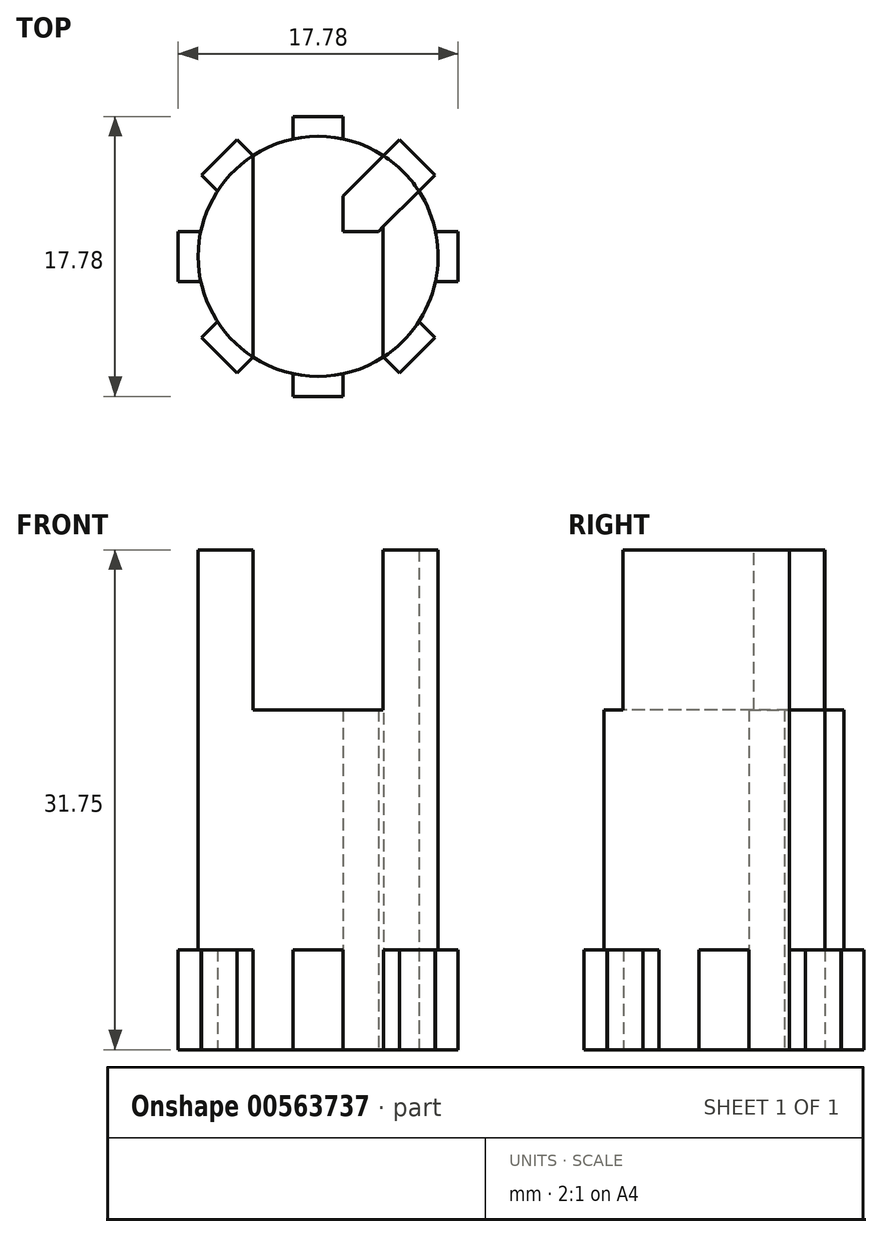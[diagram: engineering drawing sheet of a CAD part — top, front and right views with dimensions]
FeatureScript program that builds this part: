
annotation { "Feature Type Name" : "Feature", "Feature Type Description" : "" }
export const myFeature = defineFeature(function(context is Context, id is Id, definition is map)
    precondition{}
    {
        {
            var Q0;
            Q0=qCreatedBy(makeId("Top.planeOp"),FACE);
            var sketch = newSketch(context, id + "F0", { "sketchPlane" : qUnion([Q0])});
            skCircle(sketch, "E0", {"center": v(0, 0) * mm, "radius": 7.62 * mm});
            skLineSegment(sketch, "E1.bottom", {"start": v(8.9, 1.59) * mm, "end": v(-8.9, 1.59) * mm});
            skLineSegment(sketch, "E1.top", {"start": v(8.89, -1.59) * mm, "end": v(-8.89, -1.59) * mm});
            skLineSegment(sketch, "E1.left", {"start": v(8.9, 1.59) * mm, "end": v(8.9, -1.59) * mm});
            skLineSegment(sketch, "E1.right", {"start": v(-8.89, 1.59) * mm, "end": v(-8.89, -1.59) * mm});
            skLineSegment(sketch, "E2.1.0", {"start": v(7.4, -5.16) * mm, "end": v(5.16, -7.4) * mm});
            skLineSegment(sketch, "E2.1.1", {"start": v(-5.16, 7.4) * mm, "end": v(-7.4, 5.16) * mm});
            skLineSegment(sketch, "E2.1.2", {"start": v(7.4, -5.16) * mm, "end": v(-5.16, 7.4) * mm});
            skLineSegment(sketch, "E2.1.4", {"start": v(5.16, -7.4) * mm, "end": v(-7.4, 5.16) * mm});
            skLineSegment(sketch, "E2.2.0", {"start": v(1.59, -8.9) * mm, "end": v(-1.59, -8.89) * mm});
            skLineSegment(sketch, "E2.2.1", {"start": v(1.59, 8.89) * mm, "end": v(-1.59, 8.9) * mm});
            skLineSegment(sketch, "E2.2.2", {"start": v(1.59, -8.9) * mm, "end": v(1.59, 8.89) * mm});
            skLineSegment(sketch, "E2.2.4", {"start": v(-1.59, -8.89) * mm, "end": v(-1.59, 8.9) * mm});
            skLineSegment(sketch, "E2.3.0", {"start": v(-5.16, -7.4) * mm, "end": v(-7.4, -5.16) * mm});
            skLineSegment(sketch, "E2.3.1", {"start": v(7.4, 5.16) * mm, "end": v(5.16, 7.4) * mm});
            skLineSegment(sketch, "E2.3.2", {"start": v(-5.16, -7.4) * mm, "end": v(7.4, 5.16) * mm});
            skLineSegment(sketch, "E2.3.4", {"start": v(-7.4, -5.16) * mm, "end": v(5.16, 7.4) * mm});
            skLineSegment(sketch, "E2.anchor1", {"start": v(0, 0) * mm, "end": v(-8.9, -1.59) * mm, "construction": true});
            skLineSegment(sketch, "E2.anchor2", {"start": v(0, 0) * mm, "end": v(5.16, 7.4) * mm, "construction": true});
            skSolve(sketch);
        }
        {
            var Q0;
            Q0=makeQuery(id+"F0.imprint","IMPRINT",FACE,{"disambiguationData":[TD([[makeQuery(id+"F0.imprint","IMPRINT",EDGE,{"derivedFrom":sQuery(id+"F0.wireOp",EDGE,"E0")}),1.0]])]});
            var Q1;
            {var subQ0=sQuery(id+"F0.wireOp",EDGE,"E1.bottom");var subQ1=sQuery(id+"F0.wireOp",EDGE,"E0");var subQ2=makeQuery(id+"F0.imprint","INTERSECT",VERTEX,{"disambiguationData":[OD(0.0)],"derivedFrom":[subQ1,subQ0]});Q1=makeQuery(id+"F0.imprint","IMPRINT",FACE,{"disambiguationData":[TD([[makeQuery(id+"F0.imprint","IMPRINT",EDGE,{"disambiguationData":[TD([[subQ2,1.0]])],"derivedFrom":subQ1}),1.0]])]});}
            var Q2;
            {var subQ0=sQuery(id+"F0.wireOp",EDGE,"E1.top");var subQ1=sQuery(id+"F0.wireOp",EDGE,"E0");var subQ2=makeQuery(id+"F0.imprint","INTERSECT",VERTEX,{"disambiguationData":[OD(0.0)],"derivedFrom":[subQ1,subQ0]});Q2=makeQuery(id+"F0.imprint","IMPRINT",FACE,{"disambiguationData":[TD([[makeQuery(id+"F0.imprint","IMPRINT",EDGE,{"disambiguationData":[TD([[subQ2,-1.0]])],"derivedFrom":subQ1}),1.0]])]});}
            var Q3;
            {var subQ1=sQuery(id+"F0.wireOp",EDGE,"E0");var subQ7=sQuery(id+"F0.wireOp",EDGE,"E2.1.4");var subQ9=makeQuery(id+"F0.imprint","INTERSECT",VERTEX,{"disambiguationData":[OD(1.0)],"derivedFrom":[subQ1,subQ7]});Q3=makeQuery(id+"F0.imprint","IMPRINT",FACE,{"disambiguationData":[TD([[makeQuery(id+"F0.imprint","IMPRINT",EDGE,{"disambiguationData":[TD([[subQ9,-1.0]])],"derivedFrom":subQ1}),1.0]])]});}
            var Q4;
            {var subQ0=sQuery(id+"F0.wireOp",EDGE,"E2.2.4");var subQ1=sQuery(id+"F0.wireOp",EDGE,"E0");var subQ2=makeQuery(id+"F0.imprint","INTERSECT",VERTEX,{"disambiguationData":[OD(1.0)],"derivedFrom":[subQ1,subQ0]});Q4=makeQuery(id+"F0.imprint","IMPRINT",FACE,{"disambiguationData":[TD([[makeQuery(id+"F0.imprint","IMPRINT",EDGE,{"disambiguationData":[TD([[subQ2,-1.0]])],"derivedFrom":subQ1}),1.0]])]});}
            var Q5;
            {var subQ3=sQuery(id+"F0.wireOp",EDGE,"E2.3.4");var subQ5=sQuery(id+"F0.wireOp",EDGE,"E0");var subQ6=makeQuery(id+"F0.imprint","INTERSECT",VERTEX,{"disambiguationData":[OD(1.0)],"derivedFrom":[subQ5,subQ3]});Q5=makeQuery(id+"F0.imprint","IMPRINT",FACE,{"disambiguationData":[TD([[makeQuery(id+"F0.imprint","IMPRINT",EDGE,{"disambiguationData":[TD([[subQ6,-1.0]])],"derivedFrom":subQ5}),1.0]])]});}
            var Q6;
            {var subQ1=sQuery(id+"F0.wireOp",EDGE,"E1.bottom");var subQ5=sQuery(id+"F0.wireOp",EDGE,"E0");var subQ6=makeQuery(id+"F0.imprint","INTERSECT",VERTEX,{"disambiguationData":[OD(1.0)],"derivedFrom":[subQ5,subQ1]});Q6=makeQuery(id+"F0.imprint","IMPRINT",FACE,{"disambiguationData":[TD([[makeQuery(id+"F0.imprint","IMPRINT",EDGE,{"disambiguationData":[TD([[subQ6,-1.0]])],"derivedFrom":subQ5}),1.0]])]});}
            var Q7;
            {var subQ1=sQuery(id+"F0.wireOp",EDGE,"E0");var subQ7=sQuery(id+"F0.wireOp",EDGE,"E2.1.2");var subQ8=makeQuery(id+"F0.imprint","INTERSECT",VERTEX,{"disambiguationData":[OD(0.0)],"derivedFrom":[subQ1,subQ7]});Q7=makeQuery(id+"F0.imprint","IMPRINT",FACE,{"disambiguationData":[TD([[makeQuery(id+"F0.imprint","IMPRINT",EDGE,{"disambiguationData":[TD([[subQ8,-1.0]])],"derivedFrom":subQ1}),1.0]])]});}
            var Q8;
            {var subQ0=sQuery(id+"F0.wireOp",EDGE,"E2.2.2");var subQ1=sQuery(id+"F0.wireOp",EDGE,"E0");var subQ2=makeQuery(id+"F0.imprint","INTERSECT",VERTEX,{"disambiguationData":[OD(0.0)],"derivedFrom":[subQ1,subQ0]});Q8=makeQuery(id+"F0.imprint","IMPRINT",FACE,{"disambiguationData":[TD([[makeQuery(id+"F0.imprint","IMPRINT",EDGE,{"disambiguationData":[TD([[subQ2,-1.0]])],"derivedFrom":subQ1}),1.0]])]});}
            var Q9;
            {var subQ0=sQuery(id+"F0.wireOp",EDGE,"E2.3.2");var subQ1=sQuery(id+"F0.wireOp",EDGE,"E0");var subQ2=makeQuery(id+"F0.imprint","INTERSECT",VERTEX,{"disambiguationData":[OD(0.0)],"derivedFrom":[subQ1,subQ0]});Q9=makeQuery(id+"F0.imprint","IMPRINT",FACE,{"disambiguationData":[TD([[makeQuery(id+"F0.imprint","IMPRINT",EDGE,{"disambiguationData":[TD([[subQ2,-1.0]])],"derivedFrom":subQ1}),1.0]])]});}
            var Q10;
            {var subQ0=sQuery(id+"F0.wireOp",EDGE,"E2.2.2");var subQ1=sQuery(id+"F0.wireOp",EDGE,"E1.top");var subQ2=makeQuery(id+"F0.imprint","INTERSECT",VERTEX,{"derivedFrom":[subQ1,subQ0]});Q10=makeQuery(id+"F0.imprint","IMPRINT",FACE,{"disambiguationData":[TD([[makeQuery(id+"F0.imprint","IMPRINT",EDGE,{"disambiguationData":[TD([[subQ2,-1.0]])],"derivedFrom":subQ1}),1.0]])]});}
            var Q11;
            {var subQ0=sQuery(id+"F0.wireOp",EDGE,"E2.1.2");var subQ1=sQuery(id+"F0.wireOp",EDGE,"E1.top");var subQ2=makeQuery(id+"F0.imprint","INTERSECT",VERTEX,{"derivedFrom":[subQ1,subQ0]});Q11=makeQuery(id+"F0.imprint","IMPRINT",FACE,{"disambiguationData":[TD([[makeQuery(id+"F0.imprint","IMPRINT",EDGE,{"disambiguationData":[TD([[subQ2,-1.0]])],"derivedFrom":subQ1}),-1.0]])]});}
            var Q12;
            {var subQ0=sQuery(id+"F0.wireOp",EDGE,"E2.3.2");var subQ1=sQuery(id+"F0.wireOp",EDGE,"E1.bottom");var subQ2=makeQuery(id+"F0.imprint","INTERSECT",VERTEX,{"derivedFrom":[subQ1,subQ0]});Q12=makeQuery(id+"F0.imprint","IMPRINT",FACE,{"disambiguationData":[TD([[makeQuery(id+"F0.imprint","IMPRINT",EDGE,{"disambiguationData":[TD([[subQ2,-1.0]])],"derivedFrom":subQ1}),1.0]])]});}
            var Q13;
            {var subQ0=sQuery(id+"F0.wireOp",EDGE,"E2.2.2");var subQ1=sQuery(id+"F0.wireOp",EDGE,"E1.bottom");var subQ2=makeQuery(id+"F0.imprint","INTERSECT",VERTEX,{"derivedFrom":[subQ1,subQ0]});Q13=makeQuery(id+"F0.imprint","IMPRINT",FACE,{"disambiguationData":[TD([[makeQuery(id+"F0.imprint","IMPRINT",EDGE,{"disambiguationData":[TD([[subQ2,-1.0]])],"derivedFrom":subQ1}),-1.0]])]});}
            var Q14;
            {var subQ0=sQuery(id+"F0.wireOp",EDGE,"E2.2.4");var subQ1=sQuery(id+"F0.wireOp",EDGE,"E1.bottom");var subQ2=makeQuery(id+"F0.imprint","INTERSECT",VERTEX,{"derivedFrom":[subQ1,subQ0]});Q14=makeQuery(id+"F0.imprint","IMPRINT",FACE,{"disambiguationData":[TD([[makeQuery(id+"F0.imprint","IMPRINT",EDGE,{"disambiguationData":[TD([[subQ2,-1.0]])],"derivedFrom":subQ1}),1.0]])]});}
            var Q15;
            {var subQ0=sQuery(id+"F0.wireOp",EDGE,"E2.2.4");var subQ1=sQuery(id+"F0.wireOp",EDGE,"E1.top");var subQ2=makeQuery(id+"F0.imprint","INTERSECT",VERTEX,{"derivedFrom":[subQ1,subQ0]});Q15=makeQuery(id+"F0.imprint","IMPRINT",FACE,{"disambiguationData":[TD([[makeQuery(id+"F0.imprint","IMPRINT",EDGE,{"disambiguationData":[TD([[subQ2,-1.0]])],"derivedFrom":subQ1}),-1.0]])]});}
            var Q16;
            {var subQ0=sQuery(id+"F0.wireOp",EDGE,"E2.1.4");var subQ1=sQuery(id+"F0.wireOp",EDGE,"E1.top");var subQ2=makeQuery(id+"F0.imprint","INTERSECT",VERTEX,{"derivedFrom":[subQ1,subQ0]});Q16=makeQuery(id+"F0.imprint","IMPRINT",FACE,{"disambiguationData":[TD([[makeQuery(id+"F0.imprint","IMPRINT",EDGE,{"disambiguationData":[TD([[subQ2,-1.0]])],"derivedFrom":subQ1}),1.0]])]});}
            var Q17;
            {var subQ0=sQuery(id+"F0.wireOp",EDGE,"E2.1.4");var subQ1=sQuery(id+"F0.wireOp",EDGE,"E1.top");var subQ2=makeQuery(id+"F0.imprint","INTERSECT",VERTEX,{"derivedFrom":[subQ1,subQ0]});Q17=makeQuery(id+"F0.imprint","IMPRINT",FACE,{"disambiguationData":[TD([[makeQuery(id+"F0.imprint","IMPRINT",EDGE,{"disambiguationData":[TD([[subQ2,-1.0]])],"derivedFrom":subQ1}),-1.0]])]});}
            var Q18;
            {var subQ8=sQuery(id+"F0.wireOp",EDGE,"E2.1.2");var subQ11=sQuery(id+"F0.wireOp",EDGE,"E1.bottom");var subQ12=makeQuery(id+"F0.imprint","INTERSECT",VERTEX,{"derivedFrom":[subQ11,subQ8]});Q18=makeQuery(id+"F0.imprint","IMPRINT",FACE,{"disambiguationData":[TD([[makeQuery(id+"F0.imprint","IMPRINT",EDGE,{"disambiguationData":[TD([[subQ12,-1.0]])],"derivedFrom":subQ11}),1.0]])]});}
            var Q19;
            {var subQ0=sQuery(id+"F0.wireOp",EDGE,"E2.2.2");var subQ1=sQuery(id+"F0.wireOp",EDGE,"E1.top");var subQ2=makeQuery(id+"F0.imprint","INTERSECT",VERTEX,{"derivedFrom":[subQ1,subQ0]});Q19=makeQuery(id+"F0.imprint","IMPRINT",FACE,{"disambiguationData":[TD([[makeQuery(id+"F0.imprint","IMPRINT",EDGE,{"disambiguationData":[TD([[subQ2,-1.0]])],"derivedFrom":subQ1}),-1.0]])]});}
            var Q20;
            {var subQ0=sQuery(id+"F0.wireOp",EDGE,"E2.3.2");var subQ1=sQuery(id+"F0.wireOp",EDGE,"E2.1.2");var subQ2=makeQuery(id+"F0.imprint","INTERSECT",VERTEX,{"derivedFrom":[subQ1,subQ0]});Q20=makeQuery(id+"F0.imprint","IMPRINT",FACE,{"disambiguationData":[TD([[makeQuery(id+"F0.imprint","IMPRINT",EDGE,{"disambiguationData":[TD([[subQ2,-1.0]])],"derivedFrom":subQ1}),1.0]])]});}
            var Q21;
            {var subQ0=sQuery(id+"F0.wireOp",EDGE,"E2.2.2");var subQ1=sQuery(id+"F0.wireOp",EDGE,"E1.bottom");var subQ2=makeQuery(id+"F0.imprint","INTERSECT",VERTEX,{"derivedFrom":[subQ1,subQ0]});Q21=makeQuery(id+"F0.imprint","IMPRINT",FACE,{"disambiguationData":[TD([[makeQuery(id+"F0.imprint","IMPRINT",EDGE,{"disambiguationData":[TD([[subQ2,-1.0]])],"derivedFrom":subQ1}),1.0]])]});}
            var Q22;
            {var subQ0=sQuery(id+"F0.wireOp",EDGE,"E2.3.4");var subQ1=sQuery(id+"F0.wireOp",EDGE,"E1.bottom");var subQ2=makeQuery(id+"F0.imprint","INTERSECT",VERTEX,{"derivedFrom":[subQ1,subQ0]});Q22=makeQuery(id+"F0.imprint","IMPRINT",FACE,{"disambiguationData":[TD([[makeQuery(id+"F0.imprint","IMPRINT",EDGE,{"disambiguationData":[TD([[subQ2,-1.0]])],"derivedFrom":subQ1}),-1.0]])]});}
            var Q23;
            {var subQ0=sQuery(id+"F0.wireOp",EDGE,"E2.3.4");var subQ1=sQuery(id+"F0.wireOp",EDGE,"E1.bottom");var subQ2=makeQuery(id+"F0.imprint","INTERSECT",VERTEX,{"derivedFrom":[subQ1,subQ0]});Q23=makeQuery(id+"F0.imprint","IMPRINT",FACE,{"disambiguationData":[TD([[makeQuery(id+"F0.imprint","IMPRINT",EDGE,{"disambiguationData":[TD([[subQ2,-1.0]])],"derivedFrom":subQ1}),1.0]])]});}
            var Q24;
            {var subQ0=sQuery(id+"F0.wireOp",EDGE,"E2.1.2");var subQ1=sQuery(id+"F0.wireOp",EDGE,"E1.bottom");var subQ2=makeQuery(id+"F0.imprint","INTERSECT",VERTEX,{"derivedFrom":[subQ1,subQ0]});Q24=makeQuery(id+"F0.imprint","IMPRINT",FACE,{"disambiguationData":[TD([[makeQuery(id+"F0.imprint","IMPRINT",EDGE,{"disambiguationData":[TD([[subQ2,-1.0]])],"derivedFrom":subQ1}),-1.0]])]});}
            var Q25;
            {var subQ0=sQuery(id+"F0.wireOp",EDGE,"E2.2.4");var subQ1=sQuery(id+"F0.wireOp",EDGE,"E2.1.4");var subQ2=makeQuery(id+"F0.imprint","INTERSECT",VERTEX,{"derivedFrom":[subQ1,subQ0]});Q25=makeQuery(id+"F0.imprint","IMPRINT",FACE,{"disambiguationData":[TD([[makeQuery(id+"F0.imprint","IMPRINT",EDGE,{"disambiguationData":[TD([[subQ2,-1.0]])],"derivedFrom":subQ1}),-1.0]])]});}
            var Q26;
            {var subQ0=sQuery(id+"F0.wireOp",EDGE,"E2.3.2");var subQ1=sQuery(id+"F0.wireOp",EDGE,"E1.top");var subQ2=makeQuery(id+"F0.imprint","INTERSECT",VERTEX,{"derivedFrom":[subQ1,subQ0]});Q26=makeQuery(id+"F0.imprint","IMPRINT",FACE,{"disambiguationData":[TD([[makeQuery(id+"F0.imprint","IMPRINT",EDGE,{"disambiguationData":[TD([[subQ2,-1.0]])],"derivedFrom":subQ1}),1.0]])]});}
            extrude(context, id + "F1", {"entities" : qUnion([Q0, Q1, Q2, Q3, Q4, Q5, Q6, Q7, Q8, Q9, Q10, Q11, Q12, Q13, Q14, Q15, Q16, Q17, Q18, Q19, Q20, Q21, Q22, Q23, Q24, Q25, Q26]), "depth" : 31.75 * mm, "offsetDistance" : 25.4 * mm});
        }
        {
            var Q0;
            {var subQ5=sQuery(id+"F0.wireOp",EDGE,"E1.right");Q0=makeQuery(id+"F0.imprint","IMPRINT",FACE,{"disambiguationData":[TD([[makeQuery(id+"F0.imprint","IMPRINT",EDGE,{"derivedFrom":subQ5}),1.0]])]});}
            var Q1;
            {var subQ5=sQuery(id+"F0.wireOp",EDGE,"E1.left");Q1=makeQuery(id+"F0.imprint","IMPRINT",FACE,{"disambiguationData":[TD([[makeQuery(id+"F0.imprint","IMPRINT",EDGE,{"derivedFrom":subQ5}),-1.0]])]});}
            var Q2;
            {var subQ5=sQuery(id+"F0.wireOp",EDGE,"E2.1.0");Q2=makeQuery(id+"F0.imprint","IMPRINT",FACE,{"disambiguationData":[TD([[makeQuery(id+"F0.imprint","IMPRINT",EDGE,{"derivedFrom":subQ5}),-1.0]])]});}
            var Q3;
            {var subQ5=sQuery(id+"F0.wireOp",EDGE,"E2.2.0");Q3=makeQuery(id+"F0.imprint","IMPRINT",FACE,{"disambiguationData":[TD([[makeQuery(id+"F0.imprint","IMPRINT",EDGE,{"derivedFrom":subQ5}),-1.0]])]});}
            var Q4;
            {var subQ5=sQuery(id+"F0.wireOp",EDGE,"E2.3.0");Q4=makeQuery(id+"F0.imprint","IMPRINT",FACE,{"disambiguationData":[TD([[makeQuery(id+"F0.imprint","IMPRINT",EDGE,{"derivedFrom":subQ5}),-1.0]])]});}
            var Q5;
            {var subQ5=sQuery(id+"F0.wireOp",EDGE,"E2.3.1");Q5=makeQuery(id+"F0.imprint","IMPRINT",FACE,{"disambiguationData":[TD([[makeQuery(id+"F0.imprint","IMPRINT",EDGE,{"derivedFrom":subQ5}),1.0]])]});}
            var Q6;
            {var subQ5=sQuery(id+"F0.wireOp",EDGE,"E2.2.1");Q6=makeQuery(id+"F0.imprint","IMPRINT",FACE,{"disambiguationData":[TD([[makeQuery(id+"F0.imprint","IMPRINT",EDGE,{"derivedFrom":subQ5}),1.0]])]});}
            var Q7;
            {var subQ5=sQuery(id+"F0.wireOp",EDGE,"E2.1.1");Q7=makeQuery(id+"F0.imprint","IMPRINT",FACE,{"disambiguationData":[TD([[makeQuery(id+"F0.imprint","IMPRINT",EDGE,{"derivedFrom":subQ5}),1.0]])]});}
            extrude(context, id + "F2", {"entities" : qUnion([Q0, Q1, Q2, Q3, Q4, Q5, Q6, Q7]), "operationType" : NewBodyOperationType.ADD, "depth" : 6.35 * mm, "offsetDistance" : 25.4 * mm});
        }
        {
            var Q0;
            Q0=makeQuery(id+"F1.opExtrude","CAP_FACE",FACE,{"disambiguationData":[OSD([sQuery(id+"F0.wireOp",EDGE,"E0")])],"isStart":false});
            var sketch = newSketch(context, id + "F3", { "sketchPlane" : qUnion([Q0])});
            skLineSegment(sketch, "E3.bottom", {"start": v(4.13, 7.62) * mm, "end": v(-4.13, 7.62) * mm});
            skLineSegment(sketch, "E3.top", {"start": v(4.13, -7.62) * mm, "end": v(-4.13, -7.62) * mm});
            skLineSegment(sketch, "E3.left", {"start": v(4.13, 7.62) * mm, "end": v(4.13, -7.62) * mm});
            skLineSegment(sketch, "E3.right", {"start": v(-4.13, 7.62) * mm, "end": v(-4.13, -7.62) * mm});
            skPoint(sketch, "E3.middle", {"position": v(0, 0) * mm});
            skSolve(sketch);
        }
        {
            var Q0;
            {var subQ0=makeQuery(id+"F1.opExtrude","CAP_EDGE",EDGE,{"disambiguationData":[OSD([sQuery(id+"F0.wireOp",EDGE,"E0")])],"isStart":false});var subQ2=sQuery(id+"F3.wireOp",EDGE,"E3.left");var subQ3=makeQuery(id+"F3.imprint","INTERSECT",VERTEX,{"disambiguationData":[OD(0.0)],"derivedFrom":[subQ0,subQ2]});Q0=makeQuery(id+"F3.imprint","IMPRINT",FACE,{"disambiguationData":[TD([[makeQuery(id+"F3.imprint","IMPRINT",EDGE,{"disambiguationData":[TD([[subQ3,-1.0]])],"derivedFrom":subQ2}),-1.0]])]});}
            extrude(context, id + "F4", {"entities" : qUnion([Q0]), "operationType" : NewBodyOperationType.REMOVE, "oppositeDirection" : true, "depth" : 10.16 * mm, "offsetDistance" : 25.4 * mm});
        }
    });
